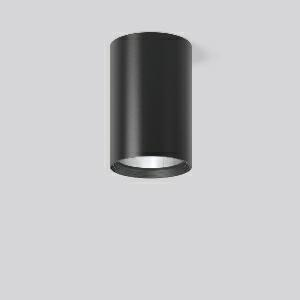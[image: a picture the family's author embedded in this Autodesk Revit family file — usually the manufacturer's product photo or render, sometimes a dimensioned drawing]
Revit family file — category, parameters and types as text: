
# Revit family: heledon_maxi_a_931219_003_1_57de
name_source: partatom
category: Lighting Fixtures
units: mm (PartAtom-declared; Revit-internal decimal feet)

## family parameters
Cut with Voids When Loaded = No
Host = Face
Light Source = No
Part Type = Normal
Room Calculation Point = No
Round Connector Dimension = Use Diameter
Shared = No

## types (1)
- HELEDON maxi A (1 x LED Modul 940, 3350 lm, 4000)
    Apparent Load = 25 VA
    Approval mark = CE
    CIE Flux Codes = 97 100 100 100 100
    Color Rendering = 92
    Color Temperature = 4000
    Default Elevation = 1800 mm
    Description = Series: HELEDON maxi
Cylindrical surface-mounted downlight. Housing: die-cast aluminium, powder-coated. Internal ceiling frame polycarbonate with bayonet mounting. Black plastic ring and recessed LED to prevent glare from the side. Optical assembly with reflector made of MIRO-Silver with 98% total light reflection for outstanding efficiency - can be changed without tools. Best colour rendering index Ra>90. Suitable for Ceiling mounting. Easy installation with a separate ceiling frame with bayonet mounting and plug connection. Driver integrated. Connected via plug-in connector. High quality converter without flickering and stroboscopic effect. The following accessories can be mounted without use of tools: interchangeable lenses, decorative glasses, honeycomb louvre, clear and frosted diffusers, white interchangeable plastic ring. 
Colour: deep black, matt (RAL 9005)
Diameter: 123 mm
Height: 183 mm
Lamp: LED
Socket: without socket
Colour temperature: 4000K
Colour rendering index (CRI): 92
System power: 25 W
Rated luminous flux: 3350 lm
Luminous efficiency: 134 lm/W
Control gear: Regulated power supply
Protection class: I
Type of protection: IP 20
    Height = 183 mm
    Lamp = 1 x LED Modul 940
    Lamp Light Flux = 3350 lm
    Lamp count = 1
    Length = 123 mm
    Lifetime = 50000 h
    Luminous efficacy = 134 lm/W
    Manufacturer = RZB
    ModVariant = No
    Model = 931219.003.1
    Mounting Place = Ceiling
    Mounting Type = Surface mounted
    Number of Poles = 1
    OnlyDefault = Yes
    Power Factor = 1
    Product Name = HELEDON maxi A
    Product group = Surface mounted downlights
    ProductGroupID = 302
    Protection Class = Protection class I
    Protection Degree = IP 20
    RLX_Detail_Level = 1
    RLX_Emergency_Light_Flux = 0 lm
    RLX_Emergency_Type = 0
    RLX_Emergency_Type_DB = No
    RlxData = <blob elided: 98821 chars, md5=1646c8c4>
    Socket = socket
    Standby Power = 0 W
    System Light Flux = 3350 lm
    System Power = 25 W
    Type Comments = Product without accessories
    Type Image = 931192.003.jpg
    URL = http://relux.com
    VarID = ---
    Voltage = 230 V
    Voltage Range = 220-240 V
    Weight = 0.00 kg
    Width = 0 mm  [stored 0 ft]

note: [stored X ft] marks values corroborated as IEEE doubles in the binary element streams (Revit-internal decimal feet)

## geometry (parser evidence)
native form markers: Blend x4, Sweep x10
no freeform markers — native parametric forms only
